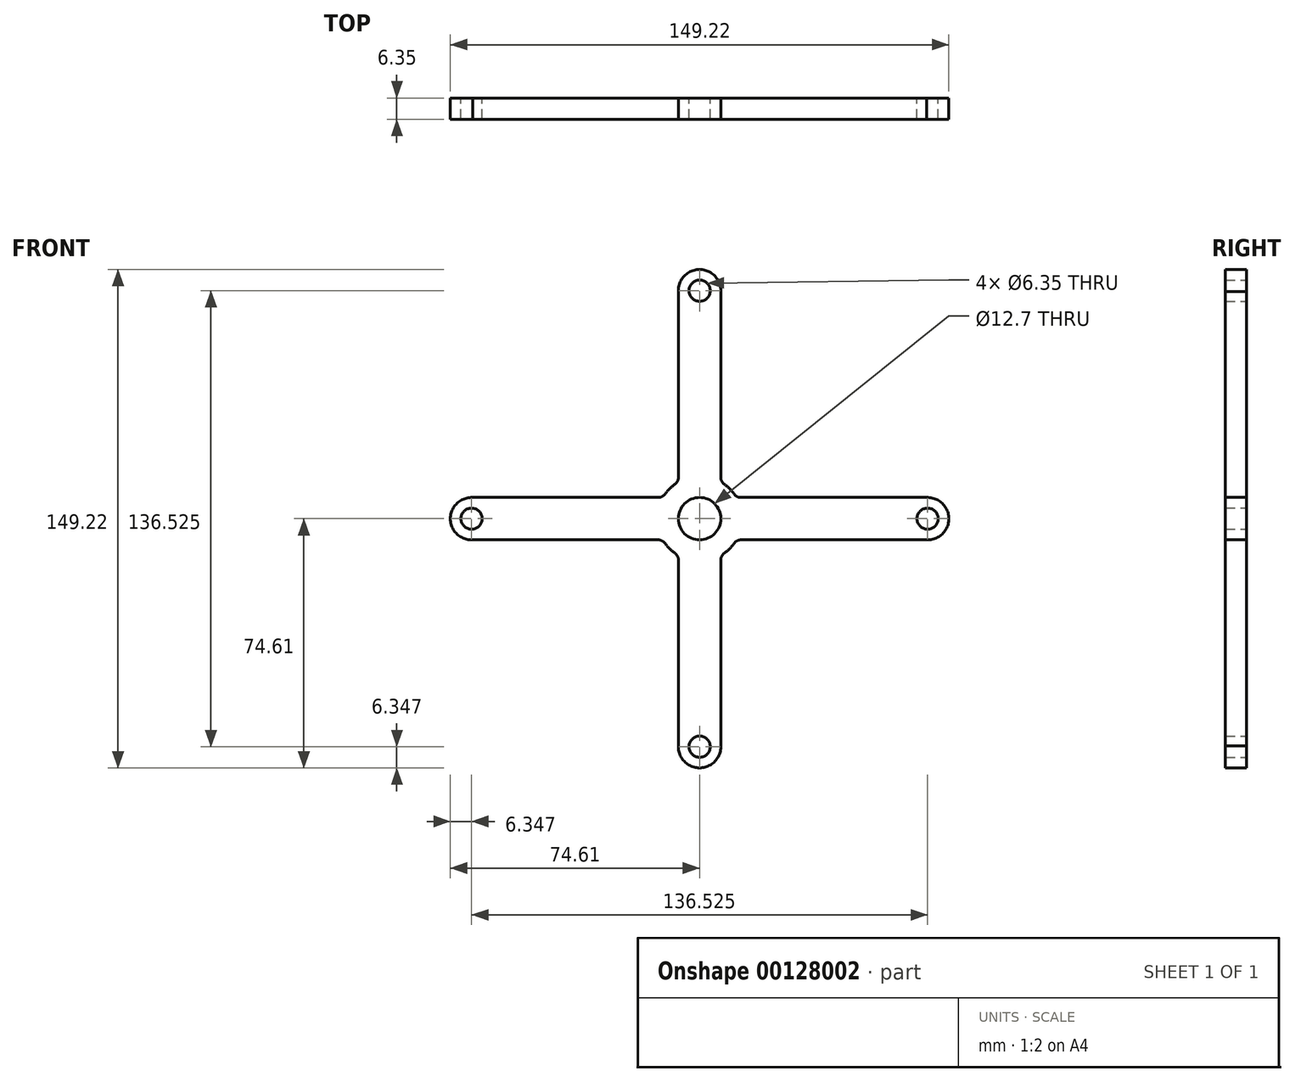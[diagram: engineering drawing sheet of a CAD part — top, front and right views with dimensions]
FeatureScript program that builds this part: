
annotation { "Feature Type Name" : "Feature", "Feature Type Description" : "" }
export const myFeature = defineFeature(function(context is Context, id is Id, definition is map)
    precondition{}
    {
        {
            var Q0;
            Q0=qCreatedBy(makeId("Front.planeOp"),FACE);
            var sketch = newSketch(context, id + "F0", { "sketchPlane" : qUnion([Q0])});
            skCircle(sketch, "E0", {"center": v(0, 68.26) * mm, "radius": 3.18 * mm});
            skArc(sketch, "E1", {"start": v(6.34, 67.97) * mm, "mid": v(0, 74.61) * mm, "end": v(-6.34, 67.97) * mm});
            skCircle(sketch, "E2", {"center": v(0, 0) * mm, "radius": 6.35 * mm});
            skArc(sketch, "E3", {"start": v(-7.4, 10.32) * mm, "mid": v(-8.98, 8.98) * mm, "end": v(-10.32, 7.4) * mm});
            skLineSegment(sketch, "E4", {"start": v(-6.34, 67.97) * mm, "end": v(-6.34, 12.38) * mm});
            skLineSegment(sketch, "E5", {"start": v(6.34, 67.97) * mm, "end": v(6.34, 12.38) * mm});
            skLineSegment(sketch, "E6.1.0", {"start": v(-67.97, 6.34) * mm, "end": v(-12.38, 6.34) * mm});
            skLineSegment(sketch, "E6.1.1", {"start": v(-67.97, -6.34) * mm, "end": v(-12.38, -6.34) * mm});
            skCircle(sketch, "E6.1.2", {"center": v(-68.26, 0) * mm, "radius": 3.18 * mm});
            skArc(sketch, "E6.1.3", {"start": v(-67.97, 6.34) * mm, "mid": v(-74.61, 0) * mm, "end": v(-67.97, -6.34) * mm});
            skLineSegment(sketch, "E6.2.0", {"start": v(-6.34, -67.97) * mm, "end": v(-6.34, -12.38) * mm});
            skLineSegment(sketch, "E6.2.1", {"start": v(6.34, -67.97) * mm, "end": v(6.34, -12.38) * mm});
            skCircle(sketch, "E6.2.2", {"center": v(0, -68.26) * mm, "radius": 3.18 * mm});
            skArc(sketch, "E6.2.3", {"start": v(-6.34, -67.97) * mm, "mid": v(0, -74.61) * mm, "end": v(6.34, -67.97) * mm});
            skLineSegment(sketch, "E6.3.0", {"start": v(67.97, -6.34) * mm, "end": v(12.38, -6.34) * mm});
            skLineSegment(sketch, "E6.3.1", {"start": v(67.97, 6.34) * mm, "end": v(12.38, 6.34) * mm});
            skCircle(sketch, "E6.3.2", {"center": v(68.26, 0) * mm, "radius": 3.18 * mm});
            skArc(sketch, "E6.3.3", {"start": v(67.97, -6.34) * mm, "mid": v(74.61, 0) * mm, "end": v(67.97, 6.34) * mm});
            skArc(sketch, "E7.trimOffspring", {"start": v(10.32, 7.4) * mm, "mid": v(8.98, 8.98) * mm, "end": v(7.4, 10.32) * mm});
            skArc(sketch, "E8.trimOffspring", {"start": v(7.4, -10.32) * mm, "mid": v(8.98, -8.98) * mm, "end": v(10.32, -7.4) * mm});
            skArc(sketch, "E9.trimOffspring", {"start": v(-10.32, -7.4) * mm, "mid": v(-8.98, -8.98) * mm, "end": v(-7.4, -10.32) * mm});
            skPoint(sketch, "E10.visualSharp", {"position": v(-6.34, 11) * mm});
            skArc(sketch, "E10.filletArc", {"start": v(-7.4, 10.32) * mm, "mid": v(-6.62, 11.22) * mm, "end": v(-6.34, 12.38) * mm});
            skPoint(sketch, "E11.visualSharp", {"position": v(-11, 6.34) * mm});
            skArc(sketch, "E11.filletArc", {"start": v(-12.38, 6.34) * mm, "mid": v(-11.22, 6.62) * mm, "end": v(-10.32, 7.4) * mm});
            skPoint(sketch, "E12.visualSharp", {"position": v(-11, -6.34) * mm});
            skArc(sketch, "E12.filletArc", {"start": v(-10.32, -7.4) * mm, "mid": v(-11.22, -6.62) * mm, "end": v(-12.38, -6.34) * mm});
            skPoint(sketch, "E13.visualSharp", {"position": v(-6.34, -11) * mm});
            skArc(sketch, "E13.filletArc", {"start": v(-6.34, -12.38) * mm, "mid": v(-6.62, -11.22) * mm, "end": v(-7.4, -10.32) * mm});
            skPoint(sketch, "E14.visualSharp", {"position": v(6.34, -11) * mm});
            skArc(sketch, "E14.filletArc", {"start": v(7.4, -10.32) * mm, "mid": v(6.62, -11.22) * mm, "end": v(6.34, -12.38) * mm});
            skPoint(sketch, "E15.visualSharp", {"position": v(11, -6.34) * mm});
            skArc(sketch, "E15.filletArc", {"start": v(12.38, -6.34) * mm, "mid": v(11.22, -6.62) * mm, "end": v(10.32, -7.4) * mm});
            skPoint(sketch, "E16.visualSharp", {"position": v(11, 6.34) * mm});
            skArc(sketch, "E16.filletArc", {"start": v(10.32, 7.4) * mm, "mid": v(11.22, 6.62) * mm, "end": v(12.38, 6.34) * mm});
            skPoint(sketch, "E17.visualSharp", {"position": v(6.34, 11) * mm});
            skArc(sketch, "E17.filletArc", {"start": v(6.34, 12.38) * mm, "mid": v(6.62, 11.22) * mm, "end": v(7.4, 10.32) * mm});
            skSolve(sketch);
        }
        {
            var Q0;
            Q0=makeQuery(id+"F0.imprint","IMPRINT",FACE,{"disambiguationData":[TD([[makeQuery(id+"F0.imprint","IMPRINT",EDGE,{"derivedFrom":sQuery(id+"F0.wireOp",EDGE,"E0")}),-1.0]])]});
            extrude(context, id + "F1", {"entities" : qUnion([Q0]), "depth" : 6.35 * mm});
        }
    });
